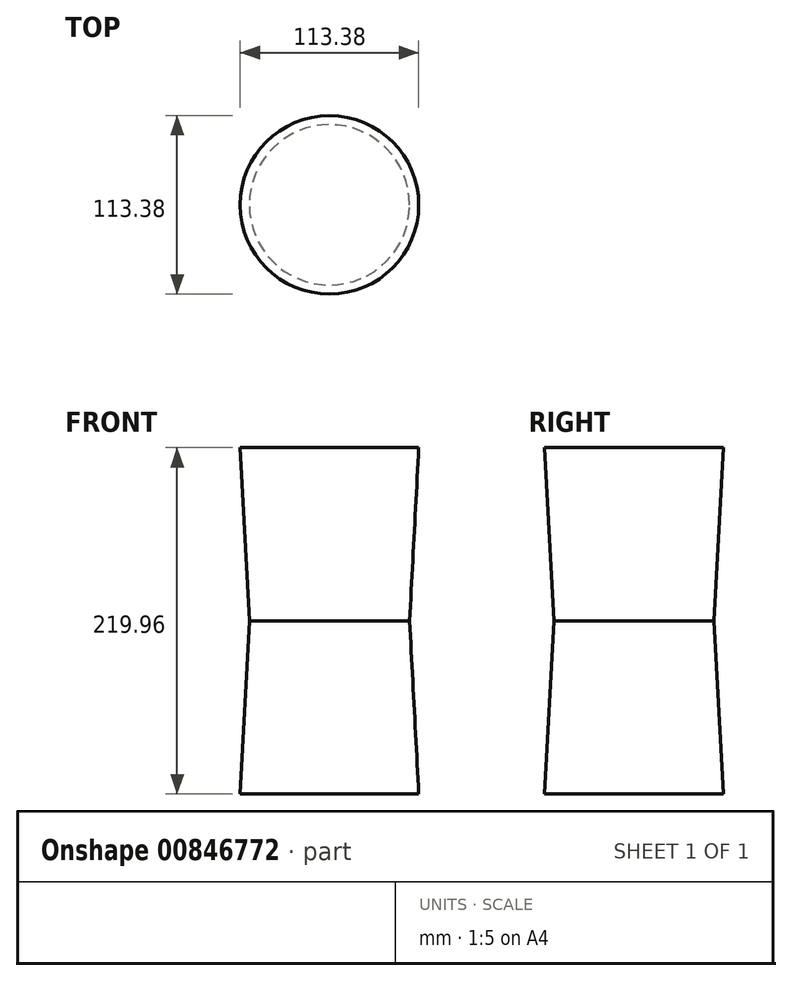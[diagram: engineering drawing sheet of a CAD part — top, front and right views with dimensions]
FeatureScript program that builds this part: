
annotation { "Feature Type Name" : "Feature", "Feature Type Description" : "" }
export const myFeature = defineFeature(function(context is Context, id is Id, definition is map)
    precondition{}
    {
        {
            var Q0;
            Q0=qCreatedBy(makeId("Top.planeOp"),FACE);
            var sketch = newSketch(context, id + "F0", { "sketchPlane" : qUnion([Q0])});
            skCircle(sketch, "E0", {"center": v(0, 0) * mm, "radius": 50.92 * mm});
            skSolve(sketch);
        }
        {
            var Q0;
            Q0=makeQuery(id+"F0.imprint","IMPRINT",FACE,{"disambiguationData":[TD([[makeQuery(id+"F0.imprint","IMPRINT",EDGE,{"derivedFrom":sQuery(id+"F0.wireOp",EDGE,"E0")}),1.0]])]});
            extrude(context, id + "F1", {"entities" : qUnion([Q0]), "depth" : 109.98 * mm, "offsetDistance" : 25.4 * mm, "hasDraft" : true, "draftAngle" : 3 * degree, "hasSecondDirection" : true, "secondDirectionOppositeDirection" : true, "secondDirectionDepth" : 109.98 * mm, "hasSecondDirectionDraft" : true, "secondDirectionDraftAngle" : 3 * degree});
        }
    });
